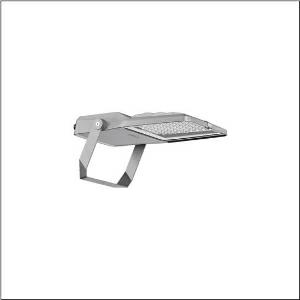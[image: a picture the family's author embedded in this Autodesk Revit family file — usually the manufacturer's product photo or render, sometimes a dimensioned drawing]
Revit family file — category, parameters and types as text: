
# Revit family: floodlight_fl_21_iq_mini___rs12_5xa7772d1b1a_349d
name_source: partatom
category: Lighting Fixtures
units: mm (PartAtom-declared; Revit-internal decimal feet)

## family parameters
Cut with Voids When Loaded = No
Host = Face
Light Source = No
Part Type = Normal
Room Calculation Point = No
Round Connector Dimension = Use Diameter
Shared = No

## types (1)
- --- (1 x LED, 14920 lm, 143 W, 2200K)
    Apparent Load = 143 VA
    CIE Flux Codes = 79 92 99 100 100
    Color Rendering = 70
    Color Temperature = 2200K
    Default Elevation = 1800 mm
    Description = Floodlight FL 21 iQ mini, floodlight, primary light control with lens, of PMMA, primary optical cover: protective disc, of toughened safety glass, transparent, light distribution: RS12, light emission: direct distribution, installation type: surface-mounted, LED, High Power LED, rated luminous flux: 14.920lm, luminous efficacy: 104lm/W, light colour: 722, colour temperature: 2200K, control gear: iQ Street-Remote/DALI, control: Street-Remote, Auto-Match, Temp-Guard, Night-Set, Smart-Wire, Desk-Remote (wireless, voltage-free reading and setting of iQ features in the workshop via application-optimized NFC function/RFID function), optimised constant luminous flux control (CLO 2.0), with terminal, 6-pole, mains connection: 220..240V, AC, 50/60Hz, start of lifetime: 143W, end of service life: 152W, reduction: 61W, luminaire housing, of diecast aluminium, powder-coated, Siteco® metallic grey (DB 702S), corrosivity category C5 mid according to DIN EN ISO 12944, suitable for swimming pools, chlorine-resistant, sealing non-destructively replaceable, mounting bracket, of steel, galvanised, powder-coated, Siteco® metallic grey (DB 702S), protection rating (complete): IP66, insulation class (complete): insulation class II (safety insulation), certification: CE, ENEC, VDE, protection symbol: D, impact resistance: IK08, permissible operating ambient temperature: -40..+40°C, permissible operating ambient temperature for outdoor applications: -40..+50°C, standard: DIN EN 12944, LABS conformity tested according to VDMA 24364:2018-05, packaging unit: 1 piece

Light Distribution: RS12
    Height = 70 mm
    Lamp = 1 x LED
    Lamp Light Flux = 14920 lm
    Lamp Power = 143 W
    Lamp count = 1
    Length = 485 mm
    Luminous efficacy = 104 lm/W
    Manufacturer = Siteco
    ModVariant = No
    Model = 5XA7772D1B1A
    Number of Poles = 1
    OnlyDefault = Yes
    Power Factor = 1
    Product Name = Floodlight FL 21 iQ mini | RS12
    Product group = floodlight | pylon annexe
    ProductGroupID = 6200
    Protection Class = Protection class II
    Protection Degree = IP 66
    RLX_Detail_Level = 1
    RLX_Emergency_Light_Flux = 0 lm
    RLX_Emergency_Type = 0
    RLX_Emergency_Type_DB = No
    RlxData = <blob elided: 91233 chars, md5=0648d848>
    Socket = socket
    Standby Power = 0 W
    System Light Flux = 14920 lm
    System Power = 143 W
    Type Comments = factory setting: luminous flux: 100 % | dim-lin: 254 | 730 mA
    Type Image = l_1006845.jpg
    URL = http://relux.com
    VarID = @adj_167414
    Voltage = 0 V
    Weight = 0.00 kg
    Width = 337 mm

## geometry (parser evidence)
native form markers: Blend x4, Sweep x14
no freeform markers — native parametric forms only
